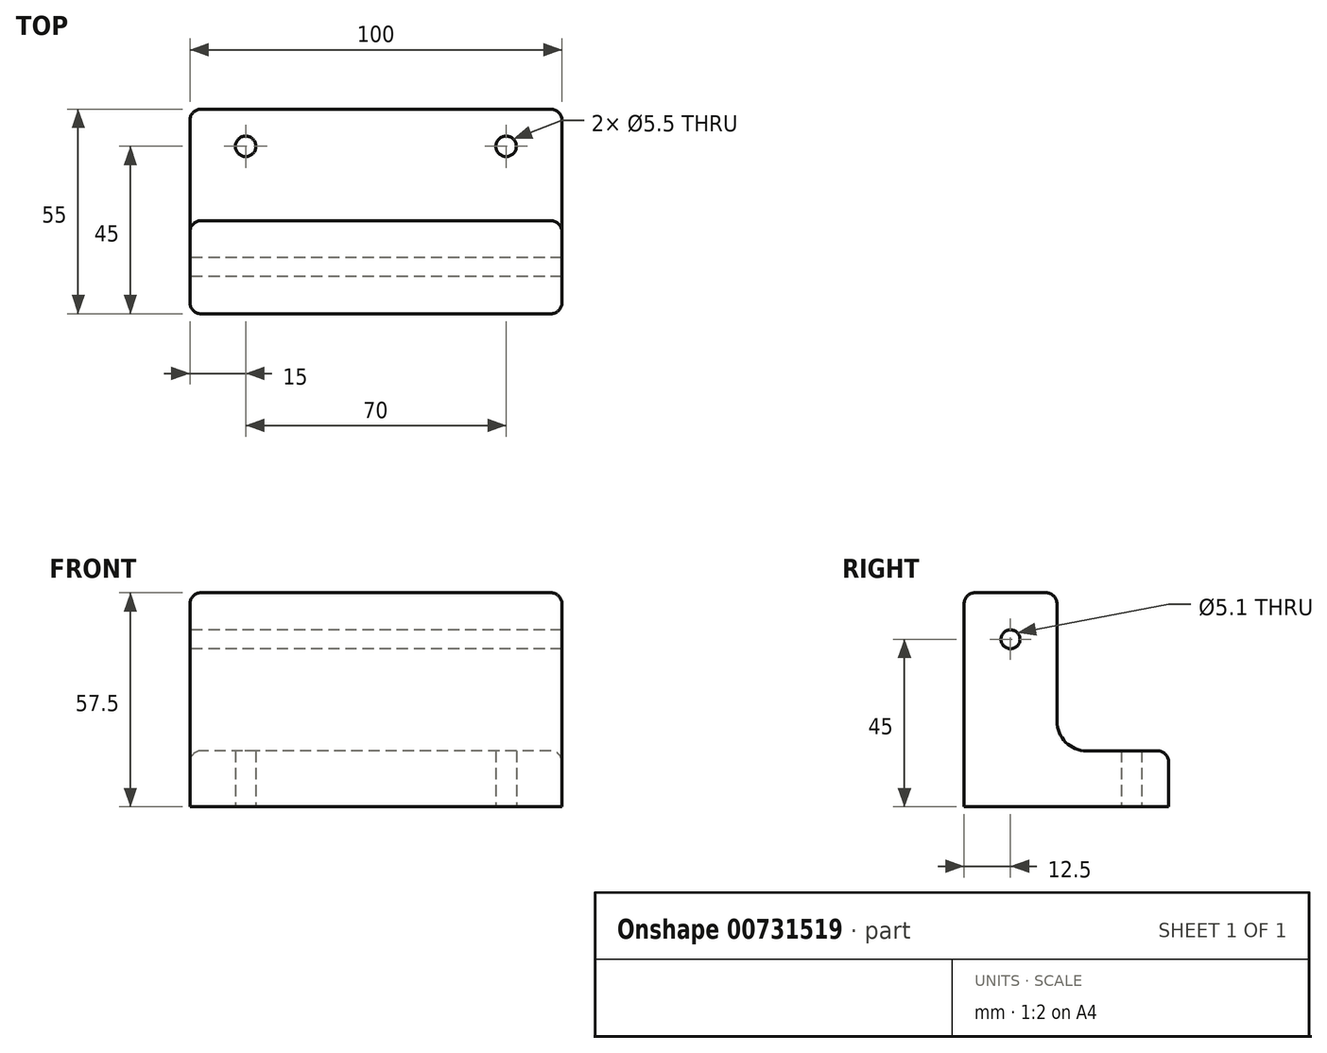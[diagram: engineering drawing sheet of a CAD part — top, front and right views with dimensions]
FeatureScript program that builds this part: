
annotation { "Feature Type Name" : "Feature", "Feature Type Description" : "" }
export const myFeature = defineFeature(function(context is Context, id is Id, definition is map)
    precondition{}
    {
        {
            var Q0;
            Q0=qCreatedBy(makeId("Right.planeOp"),FACE);
            var sketch = newSketch(context, id + "F0", { "sketchPlane" : qUnion([Q0])});
            skLineSegment(sketch, "E0", {"start": v(0, 0) * mm, "end": v(0, 57.5) * mm});
            skLineSegment(sketch, "E1", {"start": v(0, 57.5) * mm, "end": v(25, 57.5) * mm});
            skLineSegment(sketch, "E2", {"start": v(25, 57.5) * mm, "end": v(25, 23) * mm});
            skLineSegment(sketch, "E3", {"start": v(33, 15) * mm, "end": v(55, 15) * mm});
            skLineSegment(sketch, "E4", {"start": v(55, 15) * mm, "end": v(55, 0) * mm});
            skLineSegment(sketch, "E5", {"start": v(55, 0) * mm, "end": v(0, 0) * mm});
            skCircle(sketch, "E6", {"center": v(12.5, 45) * mm, "radius": 2.55 * mm});
            skPoint(sketch, "E7.visualSharp", {"position": v(25, 15) * mm});
            skArc(sketch, "E7.filletArc", {"start": v(25, 23) * mm, "mid": v(27.34, 17.34) * mm, "end": v(33, 15) * mm});
            skSolve(sketch);
        }
        {
            var Q0;
            Q0=qSketchRegion(id+"F0",true);
            extrude(context, id + "F1", {"entities" : qUnion([Q0]), "depth" : 100 * mm, "offsetDistance" : 25 * mm});
        }
        {
            var Q0;
            Q0=qCreatedBy(makeId("Top.planeOp"),FACE);
            var sketch = newSketch(context, id + "F2", { "sketchPlane" : qUnion([Q0])});
            skCircle(sketch, "E8", {"center": v(15, 45) * mm, "radius": 2.75 * mm});
            skCircle(sketch, "E9", {"center": v(85, 45) * mm, "radius": 2.75 * mm});
            skSolve(sketch);
        }
        {
            var Q0;
            Q0=qSketchRegion(id+"F2",true);
            extrude(context, id + "F3", {"entities" : qUnion([Q0]), "operationType" : NewBodyOperationType.REMOVE, "depth" : 15 * mm, "offsetDistance" : 25 * mm});
        }
        {
            var Q0;
            Q0=makeQuery(id+"F1.opExtrude","CAP_EDGE",EDGE,{"disambiguationData":[OSD([sQuery(id+"F0.wireOp",EDGE,"E1")])],"isStart":false});
            var Q1;
            Q1=makeQuery(id+"F1.opExtrude","CAP_EDGE",EDGE,{"disambiguationData":[OSD([sQuery(id+"F0.wireOp",EDGE,"E1")])],"isStart":true});
            var Q2;
            Q2=makeQuery(id+"F1.opExtrude","SWEPT_EDGE",EDGE,{"disambiguationData":[OSD([sQuery(id+"F0.wireOp",EDGE,"E1"),sQuery(id+"F0.wireOp",EDGE,"E2")])]});
            var Q3;
            Q3=makeQuery(id+"F1.opExtrude","SWEPT_EDGE",EDGE,{"disambiguationData":[OSD([sQuery(id+"F0.wireOp",EDGE,"E0"),sQuery(id+"F0.wireOp",EDGE,"E1")])]});
            var Q4;
            Q4=makeQuery(id+"F1.opExtrude","CAP_EDGE",EDGE,{"disambiguationData":[OSD([sQuery(id+"F0.wireOp",EDGE,"E3")])],"isStart":false});
            var Q5;
            Q5=makeQuery(id+"F1.opExtrude","SWEPT_EDGE",EDGE,{"disambiguationData":[OSD([sQuery(id+"F0.wireOp",EDGE,"E3"),sQuery(id+"F0.wireOp",EDGE,"E4")])]});
            var Q6;
            Q6=makeQuery(id+"F1.opExtrude","CAP_EDGE",EDGE,{"disambiguationData":[OSD([sQuery(id+"F0.wireOp",EDGE,"E3")])],"isStart":true});
            var Q7;
            Q7=makeQuery(id+"F1.opExtrude","CAP_EDGE",EDGE,{"disambiguationData":[OSD([sQuery(id+"F0.wireOp",EDGE,"E0")])],"isStart":false});
            var Q8;
            Q8=makeQuery(id+"F1.opExtrude","CAP_EDGE",EDGE,{"disambiguationData":[OSD([sQuery(id+"F0.wireOp",EDGE,"E0")])],"isStart":true});
            var Q9;
            Q9=makeQuery(id+"F1.opExtrude","CAP_EDGE",EDGE,{"disambiguationData":[OSD([sQuery(id+"F0.wireOp",EDGE,"E4")])],"isStart":true});
            var Q10;
            Q10=makeQuery(id+"F1.opExtrude","CAP_EDGE",EDGE,{"disambiguationData":[OSD([sQuery(id+"F0.wireOp",EDGE,"E4")])],"isStart":false});
            fillet(context, id + "F4", {"entities" : qUnion([Q0, Q1, Q2, Q3, Q4, Q5, Q6, Q7, Q8, Q9, Q10]), "radius" : 3 * mm, "tangentPropagation" : true, "allowEdgeOverflow" : false});
        }
    });
